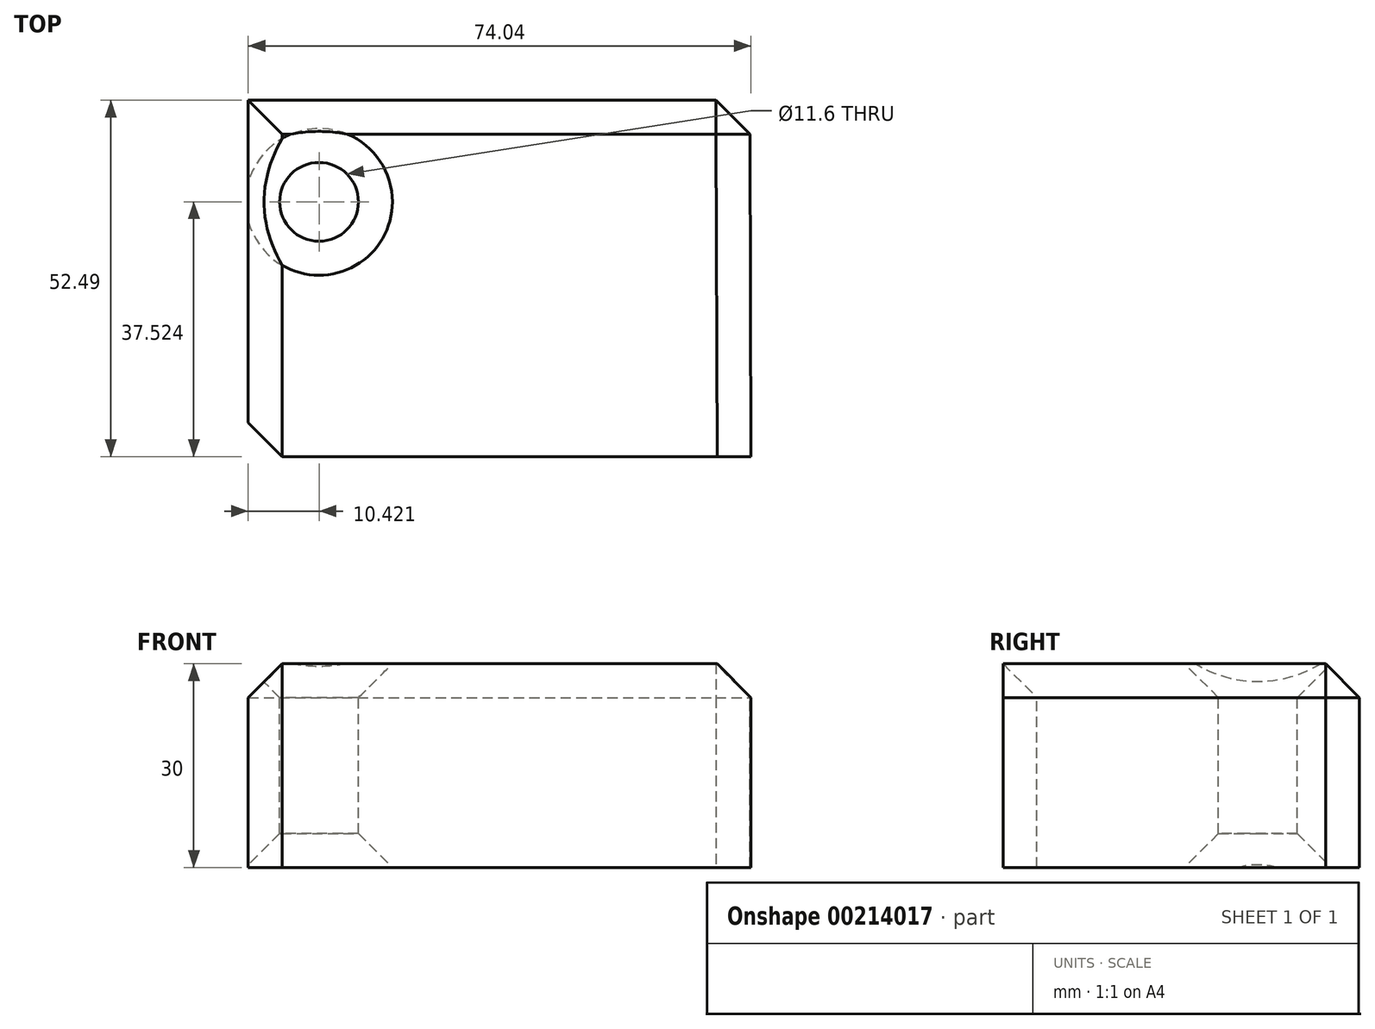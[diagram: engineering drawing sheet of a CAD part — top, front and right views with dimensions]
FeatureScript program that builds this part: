
annotation { "Feature Type Name" : "Feature", "Feature Type Description" : "" }
export const myFeature = defineFeature(function(context is Context, id is Id, definition is map)
    precondition{}
    {
        {
            var Q0;
            Q0=qCreatedBy(makeId("Top.planeOp"),FACE);
            var sketch = newSketch(context, id + "F0", { "sketchPlane" : qUnion([Q0])});
            skLineSegment(sketch, "E0", {"start": v(-37.4, 32.22) * mm, "end": v(36.43, 32.22) * mm});
            skLineSegment(sketch, "E1", {"start": v(-37.4, 32.22) * mm, "end": v(-37.4, -20.27) * mm});
            skLineSegment(sketch, "E2", {"start": v(-37.4, -20.27) * mm, "end": v(36.63, -20.27) * mm});
            skLineSegment(sketch, "E3", {"start": v(36.43, 32.22) * mm, "end": v(36.63, -20.27) * mm});
            skSolve(sketch);
        }
        {
            var Q0;
            Q0=makeQuery(id+"F0.imprint","IMPRINT",FACE,{"disambiguationData":[TD([[makeQuery(id+"F0.imprint","IMPRINT",EDGE,{"derivedFrom":sQuery(id+"F0.wireOp",EDGE,"E0")}),-1.0]])]});
            extrude(context, id + "F1", {"entities" : qUnion([Q0]), "depth" : 30 * mm});
        }
        {
            var Q0;
            Q0=makeQuery(id+"F1.opExtrude","CAP_FACE",FACE,{"disambiguationData":[OSD([sQuery(id+"F0.wireOp",EDGE,"E0"),sQuery(id+"F0.wireOp",EDGE,"E1"),sQuery(id+"F0.wireOp",EDGE,"E2"),sQuery(id+"F0.wireOp",EDGE,"E3")])],"isStart":false});
            var sketch = newSketch(context, id + "F2", { "sketchPlane" : qUnion([Q0])});
            skCircle(sketch, "E4", {"center": v(-26.99, 17.25) * mm, "radius": 5.8 * mm});
            skSolve(sketch);
        }
        {
            var Q0;
            Q0=makeQuery(id+"F2.imprint","IMPRINT",FACE,{"disambiguationData":[TD([[makeQuery(id+"F2.imprint","IMPRINT",EDGE,{"derivedFrom":sQuery(id+"F2.wireOp",EDGE,"E4")}),1.0]])]});
            extrude(context, id + "F3", {"entities" : qUnion([Q0]), "operationType" : NewBodyOperationType.REMOVE, "oppositeDirection" : true, "depth" : 30 * mm});
        }
        {
            var Q0;
            Q0=makeQuery(id+"F1.opExtrude","CAP_EDGE",EDGE,{"disambiguationData":[OSD([sQuery(id+"F0.wireOp",EDGE,"E0")])],"isStart":false});
            var Q1;
            Q1=makeQuery(id+"F1.opExtrude","SWEPT_EDGE",EDGE,{"disambiguationData":[OSD([sQuery(id+"F0.wireOp",EDGE,"E0"),sQuery(id+"F0.wireOp",EDGE,"E3")])]});
            var Q2;
            Q2=makeQuery(id+"F1.opExtrude","CAP_EDGE",EDGE,{"disambiguationData":[OSD([sQuery(id+"F0.wireOp",EDGE,"E3")])],"isStart":false});
            var Q3;
            Q3=makeQuery(id+"F1.opExtrude","CAP_EDGE",EDGE,{"disambiguationData":[OSD([sQuery(id+"F0.wireOp",EDGE,"E1")])],"isStart":false});
            var Q4;
            Q4=makeQuery(id+"F3.boolean.opBoolean","COPY",EDGE,{"derivedFrom":makeQuery(id+"F3.opExtrude","CAP_EDGE",EDGE,{"disambiguationData":[OSD([sQuery(id+"F2.wireOp",EDGE,"E4")])],"isStart":true})});
            var Q5;
            Q5=makeQuery(id+"F3.boolean.opBoolean","COPY",FACE,{"derivedFrom":makeQuery(id+"F3.opExtrude","SWEPT_FACE",FACE,{"disambiguationData":[OSD([sQuery(id+"F2.wireOp",EDGE,"E4")])]})});
            var Q6;
            Q6=makeQuery(id+"F1.opExtrude","SWEPT_EDGE",EDGE,{"disambiguationData":[OSD([sQuery(id+"F0.wireOp",EDGE,"E1"),sQuery(id+"F0.wireOp",EDGE,"E2")])]});
            chamfer(context, id + "F4", {"entities" : qUnion([Q0, Q1, Q2, Q3, Q4, Q5, Q6]), "width" : 5 * mm, "tangentPropagation" : true});
        }
    });
